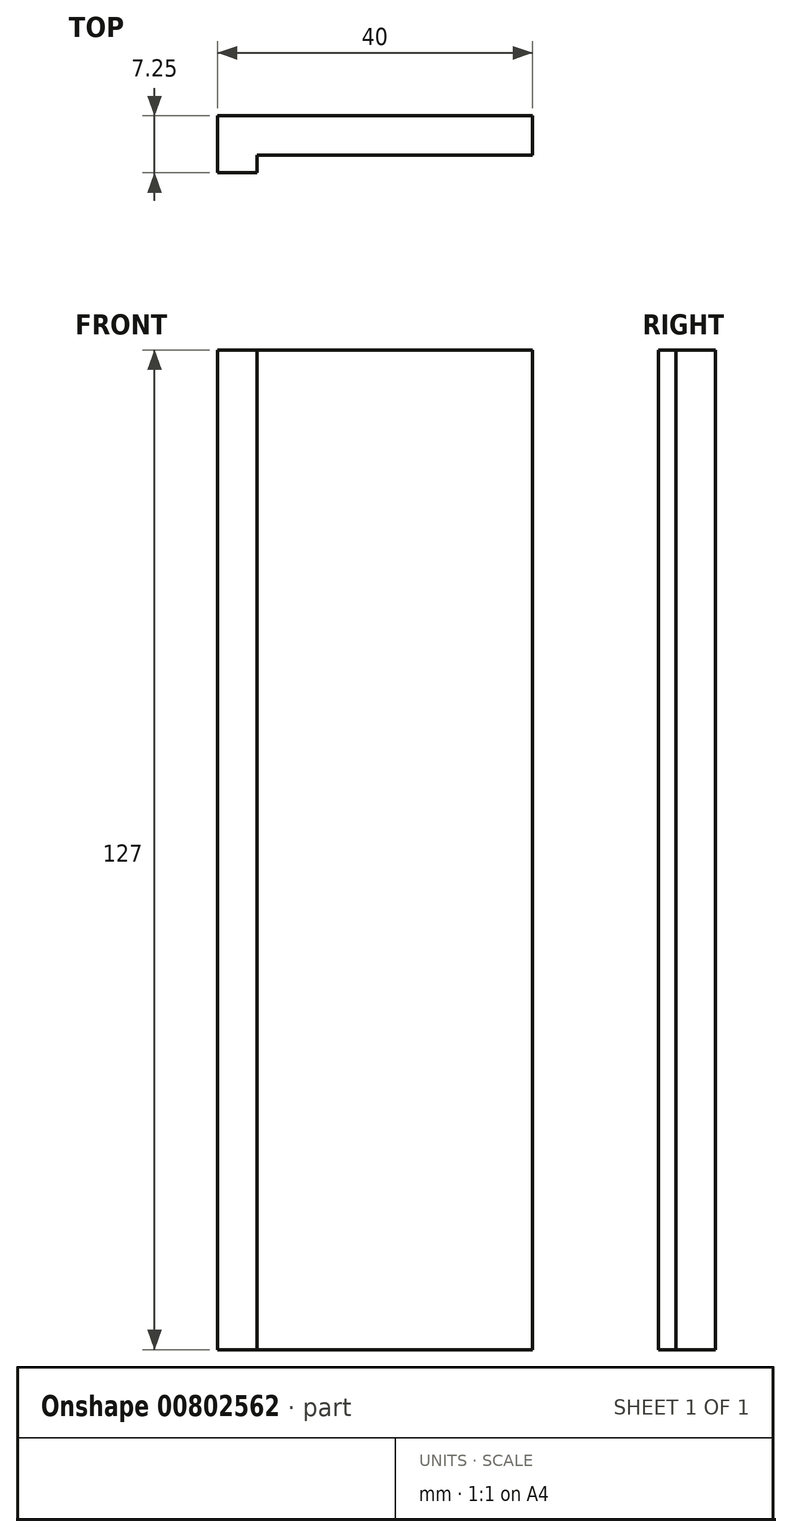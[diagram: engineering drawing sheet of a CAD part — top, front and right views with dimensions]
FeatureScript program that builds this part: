
annotation { "Feature Type Name" : "Feature", "Feature Type Description" : "" }
export const myFeature = defineFeature(function(context is Context, id is Id, definition is map)
    precondition{}
    {
        {
            var Q0;
            Q0=qCreatedBy(makeId("Top.planeOp"),FACE);
            var sketch = newSketch(context, id + "F0", { "sketchPlane" : qUnion([Q0])});
            skLineSegment(sketch, "E0.bottom", {"start": v(0, 0) * mm, "end": v(-5, 0) * mm});
            skLineSegment(sketch, "E0.top", {"start": v(0, -2.25) * mm, "end": v(-5, -2.25) * mm});
            skLineSegment(sketch, "E0.left", {"start": v(0, 0) * mm, "end": v(0, -2.25) * mm});
            skLineSegment(sketch, "E0.right", {"start": v(-5, 0) * mm, "end": v(-5, -2.25) * mm});
            skLineSegment(sketch, "E1.top", {"start": v(0, 5) * mm, "end": v(-5, 5) * mm});
            skLineSegment(sketch, "E1.left", {"start": v(0, 0) * mm, "end": v(0, 5) * mm});
            skLineSegment(sketch, "E1.right", {"start": v(-5, 0) * mm, "end": v(-5, 5) * mm});
            skLineSegment(sketch, "E2.bottom", {"start": v(0, 0) * mm, "end": v(35, 0) * mm});
            skLineSegment(sketch, "E2.top", {"start": v(0, 5) * mm, "end": v(35, 5) * mm});
            skLineSegment(sketch, "E2.right", {"start": v(35, 0) * mm, "end": v(35, 5) * mm});
            skSolve(sketch);
        }
        {
            var Q0;
            Q0 = qSketchRegion(id + "F0", true);
            extrude(context, id + "F1", {"entities" : qUnion([Q0]), "depth" : 127 * mm, "offsetDistance" : 25.4 * mm});
        }
    });
